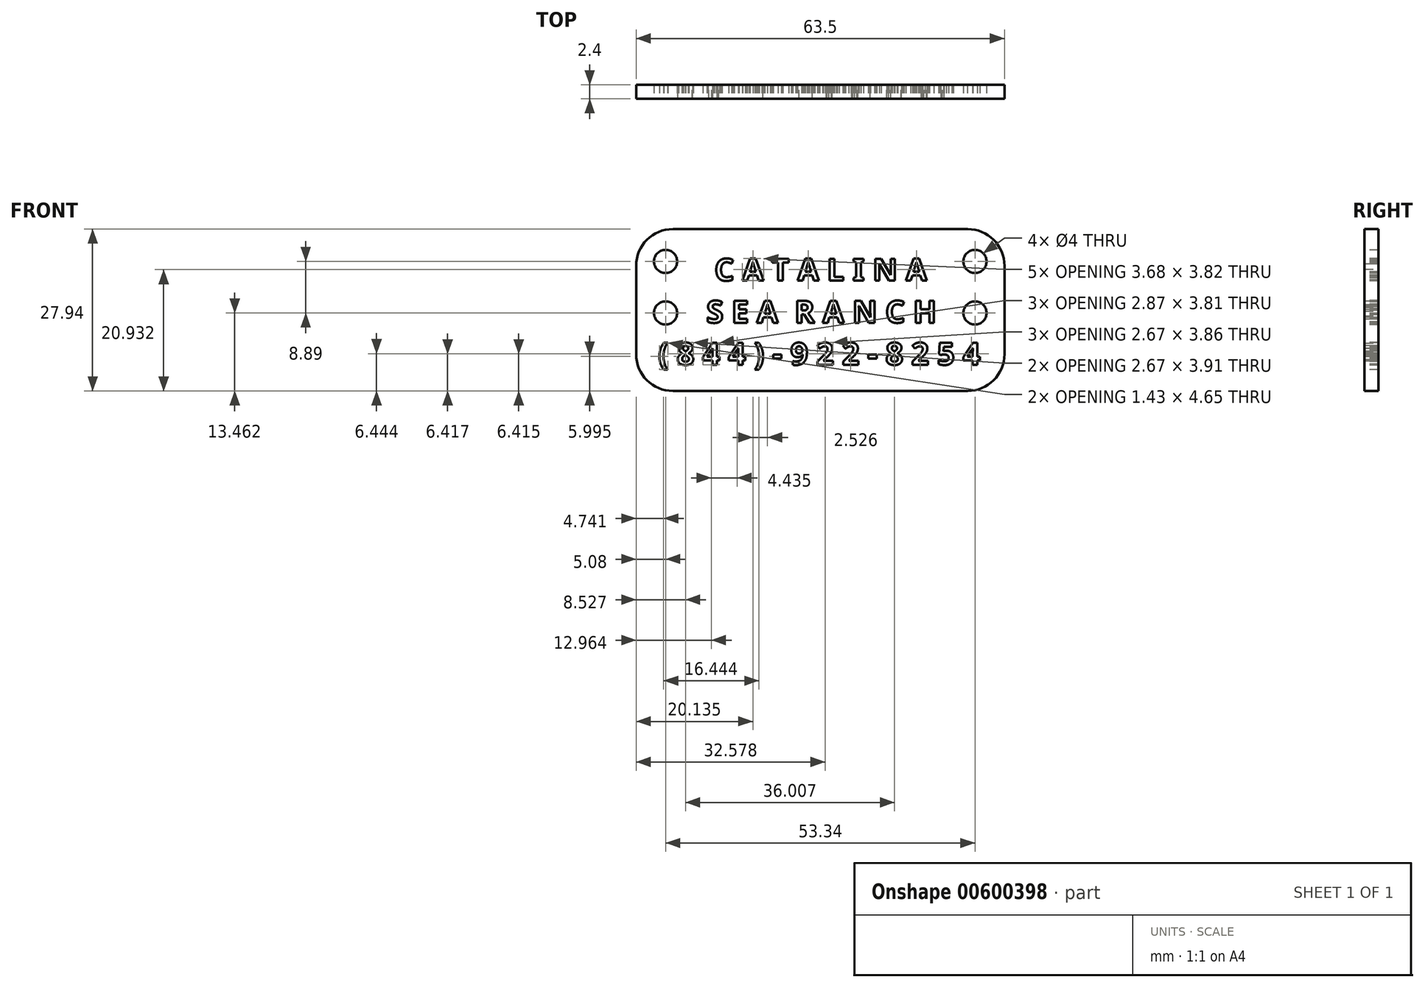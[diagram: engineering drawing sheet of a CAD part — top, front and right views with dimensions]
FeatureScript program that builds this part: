
annotation { "Feature Type Name" : "Feature", "Feature Type Description" : "" }
export const myFeature = defineFeature(function(context is Context, id is Id, definition is map)
    precondition{}
    {
        {
            var Q0;
            Q0=qCreatedBy(makeId("Front.planeOp"),FACE);
            var sketch = newSketch(context, id + "F0", { "sketchPlane" : qUnion([Q0])});
            skLineSegment(sketch, "E0.bottom", {"start": v(-25.4, 0) * mm, "end": v(25.4, 0) * mm});
            skLineSegment(sketch, "E0.top", {"start": v(-25.4, -27.94) * mm, "end": v(25.4, -27.94) * mm});
            skLineSegment(sketch, "E0.left", {"start": v(-31.75, -6.35) * mm, "end": v(-31.75, -21.6) * mm});
            skLineSegment(sketch, "E0.right", {"start": v(31.75, -6.35) * mm, "end": v(31.75, -21.6) * mm});
            skPoint(sketch, "E1.visualSharp", {"position": v(-31.75, 0) * mm});
            skArc(sketch, "E1.filletArc", {"start": v(-25.4, 0) * mm, "mid": v(-29.9, -1.86) * mm, "end": v(-31.75, -6.35) * mm});
            skPoint(sketch, "E2.visualSharp", {"position": v(-31.75, -27.94) * mm});
            skArc(sketch, "E2.filletArc", {"start": v(-31.75, -21.6) * mm, "mid": v(-29.9, -26.08) * mm, "end": v(-25.4, -27.94) * mm});
            skPoint(sketch, "E3.visualSharp", {"position": v(31.75, -27.94) * mm});
            skArc(sketch, "E3.filletArc", {"start": v(25.4, -27.94) * mm, "mid": v(29.9, -26.08) * mm, "end": v(31.75, -21.6) * mm});
            skPoint(sketch, "E4.visualSharp", {"position": v(31.75, 0) * mm});
            skArc(sketch, "E4.filletArc", {"start": v(31.75, -6.35) * mm, "mid": v(29.9, -1.86) * mm, "end": v(25.4, 0) * mm});
            skSolve(sketch);
        }
        {
            var Q0;
            Q0 = qSketchRegion(id + "F0", true);
            extrude(context, id + "F1", {"entities" : qUnion([Q0]), "depth" : 2.4 * mm, "offsetDistance" : 25.4 * mm});
        }
        {
            var Q0;
            Q0=makeQuery(id+"F1.opExtrude","CAP_FACE",FACE,{"disambiguationData":[OSD([sQuery(id+"F0.wireOp",EDGE,"E0.bottom"),sQuery(id+"F0.wireOp",EDGE,"E0.top"),sQuery(id+"F0.wireOp",EDGE,"E0.left"),sQuery(id+"F0.wireOp",EDGE,"E0.right")])],"isStart":false});
            var sketch = newSketch(context, id + "F2", { "sketchPlane" : qUnion([Q0])});
            skText(sketch, "E5", { "text": "       C A T A L I N A\n      S E A  R A N C H\n( 8 4 4 ) - 9 2 2 - 8 2 5 4", "fontName": "NotoSans-Bold.ttf"});
            skLineSegment(sketch, "E6", {"start": v(0, 0) * mm, "end": v(0, -27.94) * mm, "construction": true});
            const initialGuessF2  = {"E5": [-0.02794, -0.00892, 1, 0, 0.00384]};
            skSetInitialGuess(sketch, initialGuessF2);
            skSolve(sketch);
        }
        {
            var Q0;
            Q0 = qSketchRegion(id + "F2", true);
            extrude(context, id + "F3", {"entities" : qUnion([Q0]), "operationType" : NewBodyOperationType.REMOVE, "endBound" : BoundingType.THROUGH_ALL, "oppositeDirection" : true, "depth" : 25.4 * mm, "offsetDistance" : 25.4 * mm});
        }
        {
            var Q0;
            Q0=makeQuery(id+"F1.opExtrude","CAP_FACE",FACE,{"disambiguationData":[OSD([sQuery(id+"F0.wireOp",EDGE,"E0.bottom"),sQuery(id+"F0.wireOp",EDGE,"E0.top"),sQuery(id+"F0.wireOp",EDGE,"E0.left"),sQuery(id+"F0.wireOp",EDGE,"E0.right")])],"isStart":false});
            var sketch = newSketch(context, id + "F4", { "sketchPlane" : qUnion([Q0])});
            skCircle(sketch, "E7", {"center": v(26.67, -5.59) * mm, "radius": 2 * mm});
            skCircle(sketch, "E8", {"center": v(-26.67, -5.59) * mm, "radius": 2 * mm});
            skCircle(sketch, "E9", {"center": v(26.67, -14.48) * mm, "radius": 2 * mm});
            skCircle(sketch, "E10", {"center": v(-26.67, -14.48) * mm, "radius": 2 * mm});
            skLineSegment(sketch, "E11.bottom", {"start": v(-26.67, -5.59) * mm, "end": v(26.67, -5.59) * mm, "construction": true});
            skLineSegment(sketch, "E11.top", {"start": v(-26.67, -14.48) * mm, "end": v(26.67, -14.48) * mm, "construction": true});
            skLineSegment(sketch, "E11.left", {"start": v(-26.67, -5.59) * mm, "end": v(-26.67, -14.48) * mm, "construction": true});
            skLineSegment(sketch, "E11.right", {"start": v(26.67, -5.59) * mm, "end": v(26.67, -14.48) * mm, "construction": true});
            skLineSegment(sketch, "E12", {"start": v(0, 0) * mm, "end": v(0, -5.59) * mm});
            skSolve(sketch);
        }
        {
            var Q0;
            Q0 = qSketchRegion(id + "F4", true);
            extrude(context, id + "F5", {"entities" : qUnion([Q0]), "operationType" : NewBodyOperationType.REMOVE, "endBound" : BoundingType.THROUGH_ALL, "oppositeDirection" : true, "depth" : 25.4 * mm, "offsetDistance" : 25.4 * mm});
        }
    });
